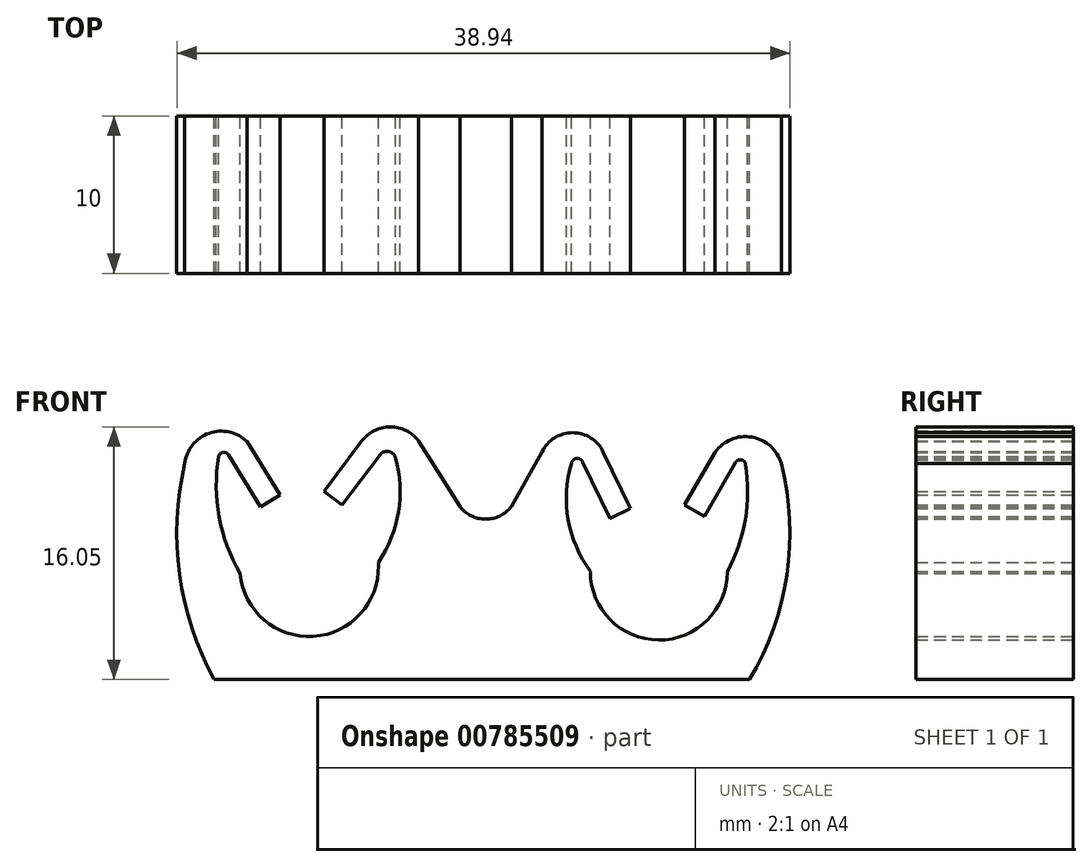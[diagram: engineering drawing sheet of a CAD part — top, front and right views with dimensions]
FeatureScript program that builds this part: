
annotation { "Feature Type Name" : "Feature", "Feature Type Description" : "" }
export const myFeature = defineFeature(function(context is Context, id is Id, definition is map)
    precondition{}
    {
        {
            var Q0;
            Q0=qCreatedBy(makeId("Front.planeOp"),FACE);
            var sketch = newSketch(context, id + "F0", { "sketchPlane" : qUnion([Q0])});
            skLineSegment(sketch, "E0", {"start": v(-24.61, -13.67) * mm, "end": v(9.39, -13.67) * mm});
            skArc(sketch, "E1", {"start": v(-22.96, -6.93) * mm, "mid": v(-18.32, -10.93) * mm, "end": v(-14.18, -6.41) * mm});
            skLineSegment(sketch, "E2", {"start": v(-14.08, 0.6) * mm, "end": v(-16.48, -2.6) * mm});
            skPoint(sketch, "E3", {"position": v(-14.08, 0.6) * mm});
            skLineSegment(sketch, "E4", {"start": v(-23.7, 0.6) * mm, "end": v(-21.67, -2.72) * mm});
            skLineSegment(sketch, "E5", {"start": v(-21.67, -2.72) * mm, "end": v(-20.43, -1.96) * mm});
            skLineSegment(sketch, "E6", {"start": v(-16.48, -2.6) * mm, "end": v(-17.64, -1.72) * mm});
            skArc(sketch, "E7", {"start": v(-24.32, 0.5) * mm, "mid": v(-24.3, -3.33) * mm, "end": v(-22.96, -6.93) * mm});
            skArc(sketch, "E8", {"start": v(-23.7, 0.6) * mm, "mid": v(-24.04, 0.76) * mm, "end": v(-24.32, 0.5) * mm});
            skLineSegment(sketch, "E9", {"start": v(-14.18, -6.41) * mm, "end": v(-14.18, -6.23) * mm});
            skArc(sketch, "E10", {"start": v(-14.18, -6.23) * mm, "mid": v(-12.9, -3.03) * mm, "end": v(-13.1, 0.4) * mm});
            skArc(sketch, "E11", {"start": v(-13.1, 0.4) * mm, "mid": v(-13.52, 0.81) * mm, "end": v(-14.08, 0.6) * mm});
            skArc(sketch, "E12", {"start": v(-1.93, 0.04) * mm, "mid": v(-2.12, -3.52) * mm, "end": v(-0.72, -6.79) * mm});
            skLineSegment(sketch, "E13", {"start": v(-1.2, 0.16) * mm, "end": v(0.54, -3.44) * mm});
            skLineSegment(sketch, "E14", {"start": v(0.54, -3.44) * mm, "end": v(1.84, -2.8) * mm});
            skLineSegment(sketch, "E15", {"start": v(8.51, 0.12) * mm, "end": v(6.52, -3.32) * mm});
            skLineSegment(sketch, "E16", {"start": v(6.52, -3.32) * mm, "end": v(5.26, -2.6) * mm});
            skArc(sketch, "E17", {"start": v(9.15, 0) * mm, "mid": v(8.87, 0.29) * mm, "end": v(8.51, 0.12) * mm});
            skArc(sketch, "E18", {"start": v(-1.2, 0.16) * mm, "mid": v(-1.61, 0.37) * mm, "end": v(-1.93, 0.04) * mm});
            skArc(sketch, "E19", {"start": v(-26.48, 0.04) * mm, "mid": v(-26.8, -6.98) * mm, "end": v(-24.61, -13.67) * mm});
            skArc(sketch, "E20", {"start": v(-0.72, -6.79) * mm, "mid": v(3.62, -11.16) * mm, "end": v(8, -6.82) * mm});
            skArc(sketch, "E21", {"start": v(8, -6.82) * mm, "mid": v(9.12, -3.5) * mm, "end": v(9.15, 0) * mm});
            skArc(sketch, "E22", {"start": v(9.39, -13.67) * mm, "mid": v(11.77, -7.02) * mm, "end": v(11.4, 0.04) * mm});
            skLineSegment(sketch, "E23", {"start": v(5.26, -2.6) * mm, "end": v(7.2, 0.76) * mm});
            skArc(sketch, "E24", {"start": v(11.4, 0.04) * mm, "mid": v(9.54, 1.73) * mm, "end": v(7.2, 0.76) * mm});
            skLineSegment(sketch, "E25", {"start": v(1.84, -2.8) * mm, "end": v(0.1, 0.8) * mm});
            skArc(sketch, "E26", {"start": v(0.1, 0.8) * mm, "mid": v(-1.84, 2.01) * mm, "end": v(-3.78, 0.8) * mm});
            skLineSegment(sketch, "E27", {"start": v(-3.78, 0.8) * mm, "end": v(-5.73, -2.67) * mm});
            skArc(sketch, "E28", {"start": v(-9, -2.67) * mm, "mid": v(-7.37, -3.48) * mm, "end": v(-5.73, -2.67) * mm});
            skLineSegment(sketch, "E29", {"start": v(-17.64, -1.72) * mm, "end": v(-15.24, 1.48) * mm});
            skLineSegment(sketch, "E30", {"start": v(-9, -2.67) * mm, "end": v(-11.62, 1.48) * mm});
            skArc(sketch, "E31", {"start": v(-11.62, 1.48) * mm, "mid": v(-13.43, 2.38) * mm, "end": v(-15.24, 1.48) * mm});
            skLineSegment(sketch, "E32", {"start": v(-20.43, -1.96) * mm, "end": v(-22.51, 1.44) * mm});
            skArc(sketch, "E33", {"start": v(-22.51, 1.44) * mm, "mid": v(-24.93, 1.98) * mm, "end": v(-26.48, 0.04) * mm});
            skSolve(sketch);
        }
        {
            var Q0;
            Q0 = qSketchRegion(id + "F0", true);
            extrude(context, id + "F1", {"entities" : qUnion([Q0]), "depth" : 10 * mm, "offsetDistance" : 25 * mm});
        }
    });
